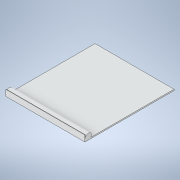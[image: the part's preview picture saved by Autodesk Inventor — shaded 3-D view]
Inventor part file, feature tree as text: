
AUTODESK INVENTOR PART (.ipt)
format: ipt  version: 2021 (Build 250183000, 183)  size: 100,352 bytes
history: imported  units: in
note: dims shown in document units (in); Inventor stores cm internally (conversion verified against a paired STEP export)
features: imported_body x1
ambient origin geometry x8: Origin, YZ Plane, XZ Plane, XY Plane, X Axis, Y Axis, Z Axis, Center Point
bodies: Solid1 (imported_parasolid), Body1 (imported_parasolid)
feature tree (1):
  imported_body  NMx_Import_Brep_tag  [imported B-rep: ~9 faces, bbox_mm=[1950.0, 150.0, 2200.0]]
